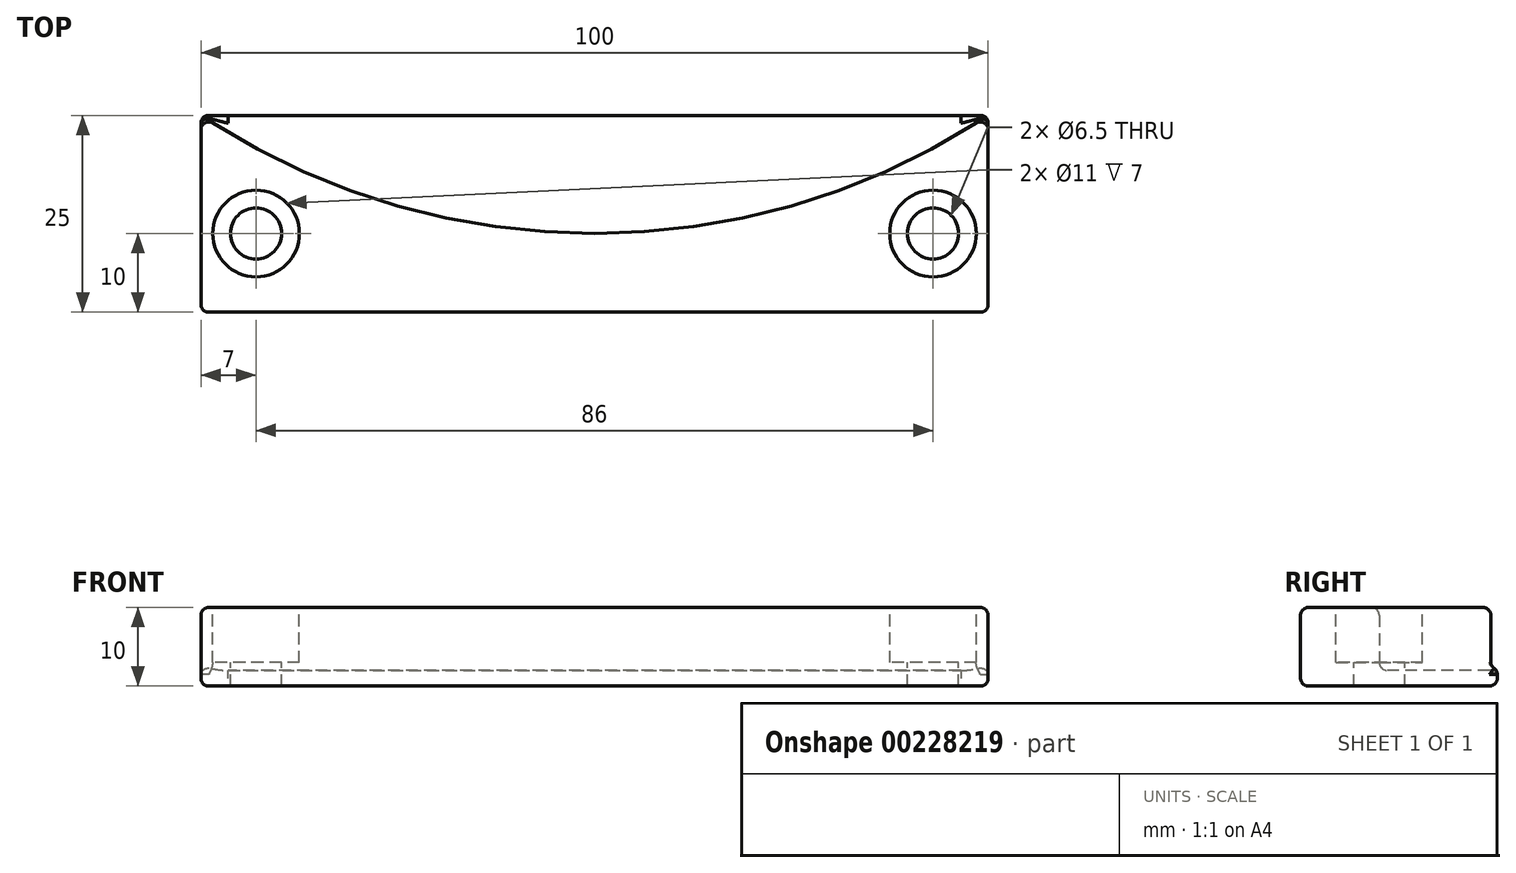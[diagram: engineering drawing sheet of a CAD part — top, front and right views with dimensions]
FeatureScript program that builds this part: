
annotation { "Feature Type Name" : "Feature", "Feature Type Description" : "" }
export const myFeature = defineFeature(function(context is Context, id is Id, definition is map)
    precondition{}
    {
        {
            var Q0;
            Q0=qCreatedBy(makeId("Top.planeOp"),FACE);
            var sketch = newSketch(context, id + "F0", { "sketchPlane" : qUnion([Q0])});
            skLineSegment(sketch, "E0.bottom", {"start": v(50, -12.5) * mm, "end": v(-50, -12.5) * mm});
            skLineSegment(sketch, "E0.top", {"start": v(50, 12.5) * mm, "end": v(-50, 12.5) * mm});
            skLineSegment(sketch, "E0.left", {"start": v(50, -12.5) * mm, "end": v(50, 12.5) * mm});
            skLineSegment(sketch, "E0.right", {"start": v(-50, -12.5) * mm, "end": v(-50, 12.5) * mm});
            skPoint(sketch, "E0.middle", {"position": v(0, 0) * mm});
            skPoint(sketch, "E1.orphan", {"position": v(0, 2.56) * mm});
            skArc(sketch, "E2", {"start": v(-50, 12.5) * mm, "mid": v(0, -2.5) * mm, "end": v(50, 12.5) * mm});
            skPoint(sketch, "E3.center.orphan", {"position": v(-43, -2.5) * mm});
            skPoint(sketch, "E4", {"position": v(43, -2.5) * mm});
            skSolve(sketch);
        }
        {
            var Q0;
            Q0=makeQuery(id+"F0.imprint","IMPRINT",FACE,{"disambiguationData":[TD([[makeQuery(id+"F0.imprint","IMPRINT",EDGE,{"derivedFrom":sQuery(id+"F0.wireOp",EDGE,"E0.bottom")}),-1.0]])]});
            extrude(context, id + "F1", {"entities" : qUnion([Q0]), "depth" : 10 * mm});
        }
        {
            var Q0;
            Q0 = qSketchRegion(id + "F0", true);
            extrude(context, id + "F2", {"entities" : qUnion([Q0]), "operationType" : NewBodyOperationType.ADD, "depth" : 2 * mm});
        }
        {
            var Q0;
            Q0=makeQuery(id+"F1.opExtrude","CAP_FACE",FACE,{"disambiguationData":[OSD([sQuery(id+"F0.wireOp",EDGE,"E0.bottom"),sQuery(id+"F0.wireOp",EDGE,"E0.left"),sQuery(id+"F0.wireOp",EDGE,"E0.right"),sQuery(id+"F0.wireOp",EDGE,"E2")])],"isStart":false});
            var sketch = newSketch(context, id + "F3", { "sketchPlane" : qUnion([Q0])});
            skPoint(sketch, "E5", {"position": v(-43, -2.5) * mm});
            skPoint(sketch, "E6", {"position": v(43, -2.5) * mm});
            skSolve(sketch);
        }
        {
            var Q0;
            Q0=sQuery(id+"F3.wireOp",VERTEX,"E5");
            var Q1;
            Q1=makeQuery(id+"F1.opExtrude","SWEPT_BODY",BODY,{"disambiguationData":[OSD([sQuery(id+"F0.wireOp",EDGE,"E0.bottom"),sQuery(id+"F0.wireOp",EDGE,"E0.left"),sQuery(id+"F0.wireOp",EDGE,"E0.right"),sQuery(id+"F0.wireOp",EDGE,"E2")])]});
            hole(context, id + "F4", {"style" : HoleStyle.C_BORE, "endStyle" : HoleEndStyle.THROUGH, "holeDiameter" : 6.5 * mm, "cBoreDiameter" : 11 * mm, "cBoreDepth" : 7 * mm, "startFromSketch" : true, "locations" : qUnion([Q0]), "scope" : qUnion([Q1]), "isTappedThrough" : true});
        }
        {
            var Q0;
            Q0=sQuery(id+"F3.wireOp",VERTEX,"E6");
            var Q1;
            Q1=makeQuery(id+"F1.opExtrude","SWEPT_BODY",BODY,{"disambiguationData":[OSD([sQuery(id+"F0.wireOp",EDGE,"E0.bottom"),sQuery(id+"F0.wireOp",EDGE,"E0.left"),sQuery(id+"F0.wireOp",EDGE,"E0.right"),sQuery(id+"F0.wireOp",EDGE,"E2")])]});
            hole(context, id + "F5", {"style" : HoleStyle.C_BORE, "endStyle" : HoleEndStyle.THROUGH, "holeDiameter" : 6.5 * mm, "cBoreDiameter" : 11 * mm, "cBoreDepth" : 7 * mm, "startFromSketch" : true, "locations" : qUnion([Q0]), "scope" : qUnion([Q1]), "isTappedThrough" : true});
        }
        {
            var Q0;
            Q0=makeQuery(id+"F1.opExtrude","CAP_EDGE",EDGE,{"disambiguationData":[OSD([sQuery(id+"F0.wireOp",EDGE,"E2")])],"isStart":false});
            var Q1;
            Q1=makeQuery(id+"F1.opExtrude","CAP_EDGE",EDGE,{"disambiguationData":[OSD([sQuery(id+"F0.wireOp",EDGE,"E0.right")])],"isStart":false});
            var Q2;
            Q2=makeQuery(id+"F1.opExtrude","CAP_EDGE",EDGE,{"disambiguationData":[OSD([sQuery(id+"F0.wireOp",EDGE,"E0.bottom")])],"isStart":false});
            var Q3;
            Q3=makeQuery(id+"F1.opExtrude","CAP_EDGE",EDGE,{"disambiguationData":[OSD([sQuery(id+"F0.wireOp",EDGE,"E0.left")])],"isStart":false});
            var Q4;
            Q4=makeQuery(id+"F4.hole-0.boolean.opBoolean","COPY",EDGE,{"derivedFrom":makeQuery(id+"F4.hole-0.opRevolve","SWEPT_EDGE",EDGE,{"disambiguationData":[OSD([sQuery(id+"F4.hole-0.sketch.wireOp",EDGE,"cbore_start_line_2"),sQuery(id+"F4.hole-0.sketch.wireOp",EDGE,"cbore_start_line_3")])]})});
            var Q5;
            Q5=makeQuery(id+"F5.hole-0.boolean.opBoolean","COPY",EDGE,{"derivedFrom":makeQuery(id+"F5.hole-0.opRevolve","SWEPT_EDGE",EDGE,{"disambiguationData":[OSD([sQuery(id+"F5.hole-0.sketch.wireOp",EDGE,"cbore_start_line_2"),sQuery(id+"F5.hole-0.sketch.wireOp",EDGE,"cbore_start_line_3")])]})});
            var Q6;
            Q6=makeQuery(id+"F2.opExtrude","CAP_FACE",FACE,{"disambiguationData":[OSD([sQuery(id+"F0.wireOp",EDGE,"E0.bottom"),sQuery(id+"F0.wireOp",EDGE,"E0.top"),sQuery(id+"F0.wireOp",EDGE,"E0.left"),sQuery(id+"F0.wireOp",EDGE,"E0.right")])],"isStart":false});
            var Q7;
            Q7=makeQuery(id+"F2.opExtrude","CAP_EDGE",EDGE,{"disambiguationData":[OSD([sQuery(id+"F0.wireOp",EDGE,"E0.top")])],"isStart":true});
            var Q8;
            Q8=makeQuery(id+"F1.opExtrude","CAP_EDGE",EDGE,{"disambiguationData":[OSD([sQuery(id+"F0.wireOp",EDGE,"E0.right")])],"isStart":true});
            var Q9;
            Q9=makeQuery(id+"F1.opExtrude","SWEPT_EDGE",EDGE,{"disambiguationData":[OSD([sQuery(id+"F0.wireOp",EDGE,"E0.bottom"),sQuery(id+"F0.wireOp",EDGE,"E0.right")])]});
            var Q10;
            {var subQ0=sQuery(id+"F0.wireOp",EDGE,"E2");var subQ1=sQuery(id+"F0.wireOp",EDGE,"E0.right");var subQ2=sQuery(id+"F0.wireOp",EDGE,"E0.top");Q10=makeQuery(id+"F2.boolean.opBoolean","MERGE",EDGE,{"derivedFrom":[makeQuery(id+"F1.opExtrude","SWEPT_EDGE",EDGE,{"disambiguationData":[OSD([subQ2,subQ1,subQ0])]}),makeQuery(id+"F2.opExtrude","SWEPT_EDGE",EDGE,{"disambiguationData":[OSD([subQ2,subQ1,subQ0])]})]});}
            var Q11;
            Q11=makeQuery(id+"F2.boolean.opBoolean","SPLIT",EDGE,{"derivedFrom":makeQuery(id+"F1.opExtrude","SWEPT_EDGE",EDGE,{"disambiguationData":[OSD([sQuery(id+"F0.wireOp",EDGE,"E0.top"),sQuery(id+"F0.wireOp",EDGE,"E0.left"),sQuery(id+"F0.wireOp",EDGE,"E2")])]})});
            var Q12;
            Q12=makeQuery(id+"F1.opExtrude","CAP_EDGE",EDGE,{"disambiguationData":[OSD([sQuery(id+"F0.wireOp",EDGE,"E0.left")])],"isStart":true});
            var Q13;
            Q13=makeQuery(id+"F1.opExtrude","CAP_EDGE",EDGE,{"disambiguationData":[OSD([sQuery(id+"F0.wireOp",EDGE,"E0.bottom")])],"isStart":true});
            var Q14;
            {var subQ0=sQuery(id+"F0.wireOp",EDGE,"E2");var subQ1=sQuery(id+"F0.wireOp",EDGE,"E0.left");var subQ2=sQuery(id+"F0.wireOp",EDGE,"E0.top");Q14=makeQuery(id+"F2.boolean.opBoolean","MERGE",EDGE,{"derivedFrom":[makeQuery(id+"F1.opExtrude","SWEPT_EDGE",EDGE,{"disambiguationData":[OSD([subQ2,subQ1,subQ0])]}),makeQuery(id+"F2.opExtrude","SWEPT_EDGE",EDGE,{"disambiguationData":[OSD([subQ2,subQ1,subQ0])]})]});}
            var Q15;
            Q15=makeQuery(id+"F1.opExtrude","SWEPT_EDGE",EDGE,{"disambiguationData":[OSD([sQuery(id+"F0.wireOp",EDGE,"E0.bottom"),sQuery(id+"F0.wireOp",EDGE,"E0.left")])]});
            var Q16;
            Q16=makeQuery(id+"F2.boolean.opBoolean","SPLIT",EDGE,{"derivedFrom":makeQuery(id+"F1.opExtrude","SWEPT_EDGE",EDGE,{"disambiguationData":[OSD([sQuery(id+"F0.wireOp",EDGE,"E0.top"),sQuery(id+"F0.wireOp",EDGE,"E0.right"),sQuery(id+"F0.wireOp",EDGE,"E2")])]})});
            var Q17;
            {var subQ0=sQuery(id+"F0.wireOp",EDGE,"E0.right");var subQ1=sQuery(id+"F0.wireOp",EDGE,"E0.left");var subQ2=sQuery(id+"F0.wireOp",EDGE,"E0.bottom");Q17=makeQuery(id+"F4.hole-0.boolean.opBoolean","INTERSECT",EDGE,{"derivedFrom":[makeQuery(id+"F2.boolean.opBoolean","MERGE",FACE,{"derivedFrom":[makeQuery(id+"F1.opExtrude","CAP_FACE",FACE,{"disambiguationData":[OSD([subQ2,subQ1,subQ0,sQuery(id+"F0.wireOp",EDGE,"E2")])],"isStart":true}),makeQuery(id+"F2.opExtrude","CAP_FACE",FACE,{"disambiguationData":[OSD([subQ2,sQuery(id+"F0.wireOp",EDGE,"E0.top"),subQ1,subQ0])],"isStart":true})]}),makeQuery(id+"F4.hole-0.opRevolve","SWEPT_FACE",FACE,{"disambiguationData":[OSD([sQuery(id+"F4.hole-0.sketch.wireOp",EDGE,"core_line_2")])]})]});}
            var Q18;
            Q18=makeQuery(id+"F5.hole-0.boolean.opBoolean","COPY",FACE,{"derivedFrom":makeQuery(id+"F5.hole-0.opRevolve","SWEPT_FACE",FACE,{"disambiguationData":[OSD([sQuery(id+"F5.hole-0.sketch.wireOp",EDGE,"core_line_2")])]})});
            var Q19;
            Q19=makeQuery(id+"F4.hole-0.boolean.opBoolean","COPY",EDGE,{"derivedFrom":makeQuery(id+"F4.hole-0.opRevolve","SWEPT_EDGE",EDGE,{"disambiguationData":[OSD([sQuery(id+"F4.hole-0.sketch.wireOp",EDGE,"cbore_start_line_1"),sQuery(id+"F4.hole-0.sketch.wireOp",EDGE,"core_line_2")])]})});
            fillet(context, id + "F6", {"entities" : qUnion([Q0, Q1, Q2, Q3, Q4, Q5, Q6, Q7, Q8, Q9, Q10, Q11, Q12, Q13, Q14, Q15, Q16, Q17, Q18, Q19]), "radius" : 1 * mm, "tangentPropagation" : true, "allowEdgeOverflow" : false});
        }
    });
